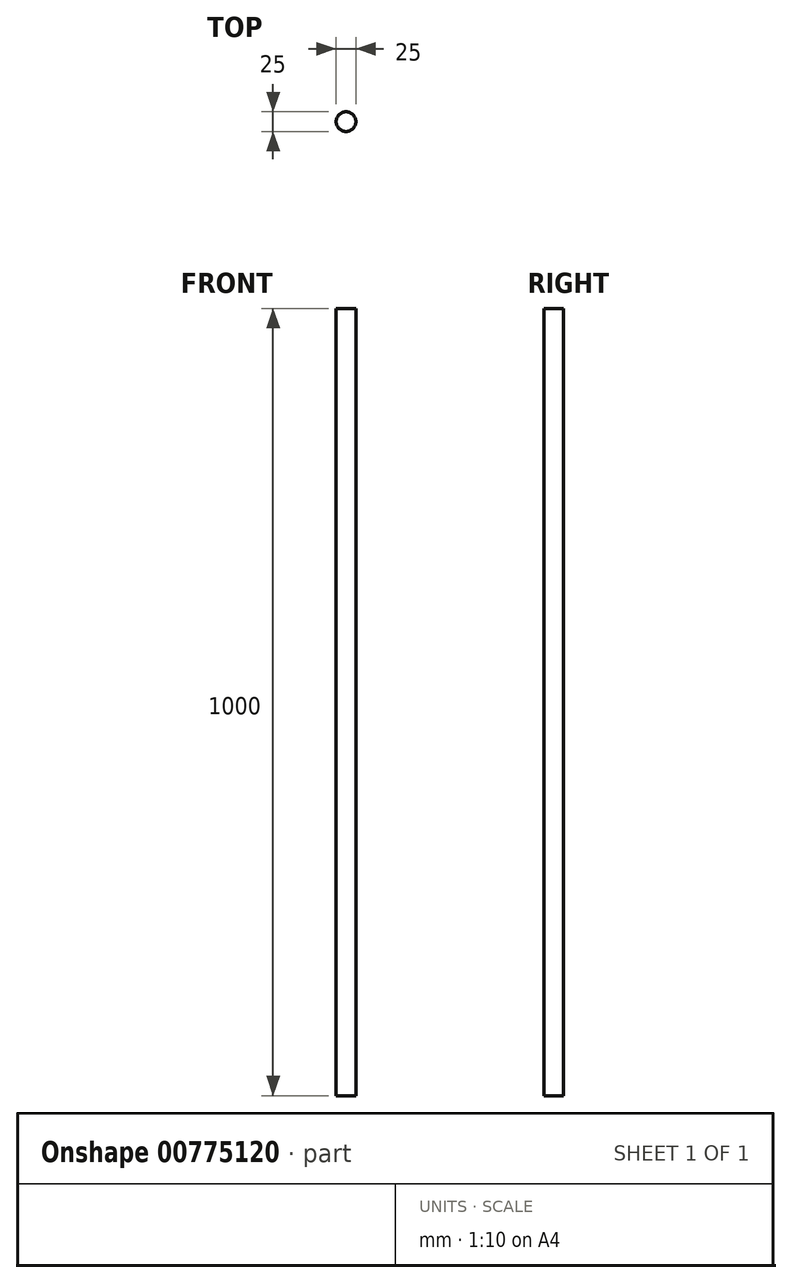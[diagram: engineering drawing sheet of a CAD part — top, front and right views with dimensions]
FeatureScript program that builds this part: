
annotation { "Feature Type Name" : "Feature", "Feature Type Description" : "" }
export const myFeature = defineFeature(function(context is Context, id is Id, definition is map)
    precondition{}
    {
        {
            var Q0;
            Q0=qCreatedBy(makeId("Top.planeOp"),FACE);
            var sketch = newSketch(context, id + "F0", { "sketchPlane" : qUnion([Q0])});
            skCircle(sketch, "E0", {"center": v(0, 0) * mm, "radius": 12.5 * mm});
            skSolve(sketch);
        }
        {
            var Q0;
            Q0 = qSketchRegion(id + "F0", true);
            extrude(context, id + "F1", {"entities" : qUnion([Q0]), "depth" : 1000 * mm, "offsetDistance" : 25 * mm});
        }
    });
